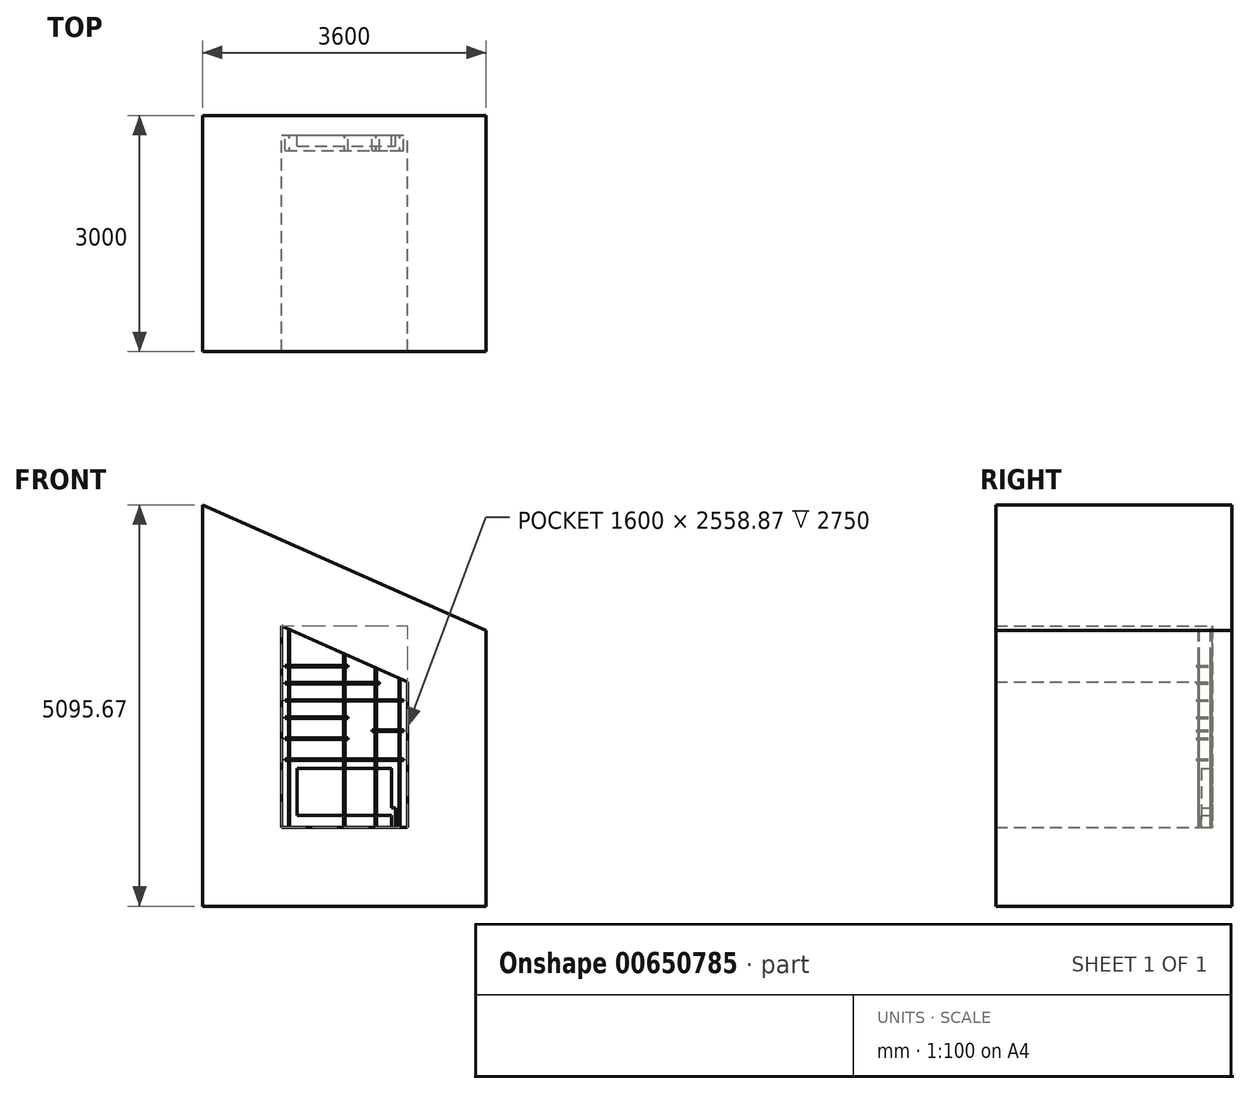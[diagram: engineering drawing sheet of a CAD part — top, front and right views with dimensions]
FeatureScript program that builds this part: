
annotation { "Feature Type Name" : "Feature", "Feature Type Description" : "" }
export const myFeature = defineFeature(function(context is Context, id is Id, definition is map)
    precondition{}
    {
        {
            var Q0;
            Q0=qCreatedBy(makeId("Front.planeOp"),FACE);
            var sketch = newSketch(context, id + "F0", { "sketchPlane" : qUnion([Q0])});
            skLineSegment(sketch, "E0", {"start": v(0, 0) * mm, "end": v(1600, 0) * mm});
            skLineSegment(sketch, "E1", {"start": v(0, 0) * mm, "end": v(0, 2558.87) * mm});
            skLineSegment(sketch, "E2", {"start": v(0, 2558.87) * mm, "end": v(1600, 1850) * mm});
            skLineSegment(sketch, "E3", {"start": v(1600, 1850) * mm, "end": v(1600, 0) * mm});
            skLineSegment(sketch, "E4.0", {"start": v(2600, 2500.7) * mm, "end": v(2600, -1000) * mm});
            skLineSegment(sketch, "E4.1", {"start": v(-1000, 4095.67) * mm, "end": v(2600, 2500.7) * mm});
            skLineSegment(sketch, "E4.2", {"start": v(-1000, -1000) * mm, "end": v(-1000, 4095.67) * mm});
            skLineSegment(sketch, "E4.3", {"start": v(-1000, -1000) * mm, "end": v(2600, -1000) * mm});
            skSolve(sketch);
        }
        {
            var Q0;
            Q0=makeQuery(id+"F0.imprint","IMPRINT",FACE,{"disambiguationData":[TD([[makeQuery(id+"F0.imprint","IMPRINT",EDGE,{"derivedFrom":sQuery(id+"F0.wireOp",EDGE,"E0")}),-1.0]])]});
            extrude(context, id + "F1", {"entities" : qUnion([Q0]), "depth" : 3000 * mm, "offsetDistance" : 25 * mm});
        }
        {
            var Q0;
            Q0=makeQuery(id+"F0.imprint","IMPRINT",FACE,{"disambiguationData":[TD([[makeQuery(id+"F0.imprint","IMPRINT",EDGE,{"derivedFrom":sQuery(id+"F0.wireOp",EDGE,"E0")}),1.0]])]});
            extrude(context, id + "F2", {"entities" : qUnion([Q0]), "operationType" : NewBodyOperationType.ADD, "depth" : 250 * mm, "offsetDistance" : 25 * mm});
        }
        {
            var Q0;
            Q0=makeQuery(id+"F2.opExtrude","CAP_FACE",FACE,{"disambiguationData":[OSD([sQuery(id+"F0.wireOp",EDGE,"E0"),sQuery(id+"F0.wireOp",EDGE,"E1"),sQuery(id+"F0.wireOp",EDGE,"E2"),sQuery(id+"F0.wireOp",EDGE,"E3")])],"isStart":false});
            var sketch = newSketch(context, id + "F3", { "sketchPlane" : qUnion([Q0])});
            skLineSegment(sketch, "E5.bottom", {"start": v(200, 750) * mm, "end": v(1400, 750) * mm});
            skLineSegment(sketch, "E5.top", {"start": v(200, 150) * mm, "end": v(1400, 150) * mm});
            skLineSegment(sketch, "E5.left", {"start": v(200, 750) * mm, "end": v(200, 150) * mm});
            skLineSegment(sketch, "E5.right", {"start": v(1400, 750) * mm, "end": v(1400, 250) * mm});
            skLineSegment(sketch, "E6", {"start": v(1400, 250) * mm, "end": v(1450, 250) * mm});
            skLineSegment(sketch, "E7", {"start": v(1450, 250) * mm, "end": v(1450, 0) * mm});
            skLineSegment(sketch, "E8", {"start": v(1450, 0) * mm, "end": v(1400, 0) * mm});
            skLineSegment(sketch, "E9", {"start": v(1400, 0) * mm, "end": v(1400, 150) * mm});
            skSolve(sketch);
        }
        {
            var Q0;
            Q0=makeQuery(id+"F3.imprint","IMPRINT",FACE,{"disambiguationData":[TD([[makeQuery(id+"F3.imprint","IMPRINT",EDGE,{"derivedFrom":sQuery(id+"F3.wireOp",EDGE,"E5.bottom")}),-1.0]])]});
            extrude(context, id + "F4", {"entities" : qUnion([Q0]), "depth" : 140 * mm, "offsetDistance" : 25 * mm});
        }
        {
            var Q0;
            Q0=makeQuery(id+"F2.opExtrude","CAP_FACE",FACE,{"disambiguationData":[OSD([sQuery(id+"F0.wireOp",EDGE,"E0"),sQuery(id+"F0.wireOp",EDGE,"E1"),sQuery(id+"F0.wireOp",EDGE,"E2"),sQuery(id+"F0.wireOp",EDGE,"E3")])],"isStart":false});
            var sketch = newSketch(context, id + "F5", { "sketchPlane" : qUnion([Q0])});
            skLineSegment(sketch, "E10.bottom", {"start": v(50, 868) * mm, "end": v(1550, 868) * mm});
            skLineSegment(sketch, "E10.top", {"start": v(50, 850) * mm, "end": v(1550, 850) * mm});
            skLineSegment(sketch, "E10.left", {"start": v(50, 868) * mm, "end": v(50, 850) * mm});
            skLineSegment(sketch, "E10.right", {"start": v(1550, 868) * mm, "end": v(1550, 850) * mm});
            skPoint(sketch, "E11", {"position": v(800, 0) * mm});
            skPoint(sketch, "E12", {"position": v(800, 850) * mm});
            skLineSegment(sketch, "E13.bottom", {"start": v(1150, 1236) * mm, "end": v(1550, 1236) * mm});
            skLineSegment(sketch, "E13.top", {"start": v(1150, 1218) * mm, "end": v(1550, 1218) * mm});
            skLineSegment(sketch, "E13.left", {"start": v(1150, 1236) * mm, "end": v(1150, 1218) * mm});
            skLineSegment(sketch, "E13.right", {"start": v(1550, 1236) * mm, "end": v(1550, 1218) * mm});
            skLineSegment(sketch, "E14.bottom", {"start": v(50, 1136) * mm, "end": v(850, 1136) * mm});
            skLineSegment(sketch, "E14.top", {"start": v(50, 1118) * mm, "end": v(850, 1118) * mm});
            skLineSegment(sketch, "E14.left", {"start": v(50, 1136) * mm, "end": v(50, 1118) * mm});
            skLineSegment(sketch, "E14.right", {"start": v(850, 1136) * mm, "end": v(850, 1118) * mm});
            skLineSegment(sketch, "E15.bottom", {"start": v(50, 1404) * mm, "end": v(850, 1404) * mm});
            skLineSegment(sketch, "E15.top", {"start": v(50, 1386) * mm, "end": v(850, 1386) * mm});
            skLineSegment(sketch, "E15.left", {"start": v(50, 1404) * mm, "end": v(50, 1386) * mm});
            skLineSegment(sketch, "E15.right", {"start": v(850, 1404) * mm, "end": v(850, 1386) * mm});
            skLineSegment(sketch, "E16.bottom", {"start": v(50, 1622) * mm, "end": v(1550, 1622) * mm});
            skLineSegment(sketch, "E16.top", {"start": v(50, 1604) * mm, "end": v(1550, 1604) * mm});
            skLineSegment(sketch, "E16.left", {"start": v(50, 1622) * mm, "end": v(50, 1604) * mm});
            skLineSegment(sketch, "E16.right", {"start": v(1550, 1622) * mm, "end": v(1550, 1604) * mm});
            skPoint(sketch, "E17", {"position": v(800, 1604) * mm});
            skLineSegment(sketch, "E18.bottom", {"start": v(50, 2058) * mm, "end": v(850, 2058) * mm});
            skLineSegment(sketch, "E18.top", {"start": v(50, 2040) * mm, "end": v(850, 2040) * mm});
            skLineSegment(sketch, "E18.left", {"start": v(50, 2058) * mm, "end": v(50, 2040) * mm});
            skLineSegment(sketch, "E18.right", {"start": v(850, 2058) * mm, "end": v(850, 2040) * mm});
            skLineSegment(sketch, "E19.bottom", {"start": v(50, 1840) * mm, "end": v(1250, 1840) * mm});
            skLineSegment(sketch, "E19.top", {"start": v(50, 1822) * mm, "end": v(1250, 1822) * mm});
            skLineSegment(sketch, "E19.left", {"start": v(50, 1840) * mm, "end": v(50, 1822) * mm});
            skLineSegment(sketch, "E19.right", {"start": v(1250, 1840) * mm, "end": v(1250, 1822) * mm});
            skPoint(sketch, "E20", {"position": v(650, 1822) * mm});
            skSolve(sketch);
        }
        {
            var Q0;
            Q0 = qSketchRegion(id + "F5", true);
            extrude(context, id + "F6", {"entities" : qUnion([Q0]), "depth" : 200 * mm, "offsetDistance" : 25 * mm});
        }
        {
            var Q0;
            Q0=makeQuery(id+"F1.opExtrude","SWEPT_FACE",FACE,{"disambiguationData":[OSD([sQuery(id+"F0.wireOp",EDGE,"E0")])]});
            var sketch = newSketch(context, id + "F7", { "sketchPlane" : qUnion([Q0])});
            skCircle(sketch, "E21", {"center": v(100, -275) * mm, "radius": 7 * mm});
            skPoint(sketch, "E22", {"position": v(0, -250) * mm});
            skCircle(sketch, "E23", {"center": v(100, -425) * mm, "radius": 7 * mm});
            skCircle(sketch, "E24.1.0.0", {"center": v(1500, -425) * mm, "radius": 7 * mm});
            skCircle(sketch, "E24.1.0.1", {"center": v(1500, -275) * mm, "radius": 7 * mm});
            skLineSegment(sketch, "E24.direction1", {"start": v(100, -425) * mm, "end": v(1500, -425) * mm, "construction": true});
            skCircle(sketch, "E25.1.0.0", {"center": v(800, -275) * mm, "radius": 7 * mm});
            skCircle(sketch, "E25.1.0.1", {"center": v(800, -425) * mm, "radius": 7 * mm});
            skLineSegment(sketch, "E25.direction1", {"start": v(100, -425) * mm, "end": v(800, -425) * mm, "construction": true});
            skCircle(sketch, "E26.1.0.0", {"center": v(1200, -275) * mm, "radius": 7 * mm});
            skCircle(sketch, "E26.1.0.1", {"center": v(1200, -425) * mm, "radius": 7 * mm});
            skLineSegment(sketch, "E26.direction1", {"start": v(100, -425) * mm, "end": v(1200, -425) * mm, "construction": true});
            skSolve(sketch);
        }
        {
            var Q0;
            Q0 = qSketchRegion(id + "F7", true);
            var Q1;
            Q1=makeQuery(id+"F1.opExtrude","SWEPT_FACE",FACE,{"disambiguationData":[OSD([sQuery(id+"F0.wireOp",EDGE,"E2")])]});
            extrude(context, id + "F8", {"entities" : qUnion([Q0]), "endBound" : BoundingType.UP_TO_SURFACE, "depth" : 3000 * mm, "endBoundEntityFace" : qUnion([Q1]), "offsetDistance" : 25 * mm});
        }
    });
